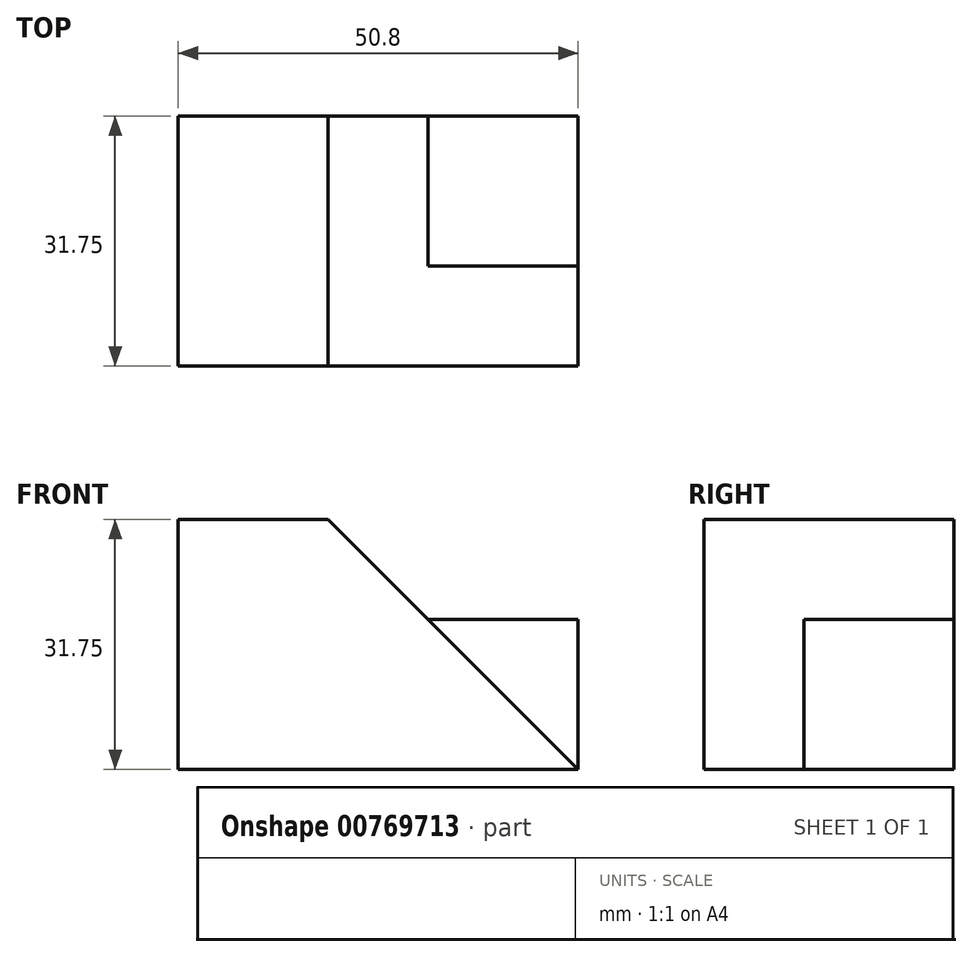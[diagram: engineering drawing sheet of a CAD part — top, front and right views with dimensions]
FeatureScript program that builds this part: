
annotation { "Feature Type Name" : "Feature", "Feature Type Description" : "" }
export const myFeature = defineFeature(function(context is Context, id is Id, definition is map)
    precondition{}
    {
        {
            var Q0;
            Q0=qCreatedBy(makeId("Front.planeOp"),FACE);
            var sketch = newSketch(context, id + "F0", { "sketchPlane" : qUnion([Q0])});
            skLineSegment(sketch, "E0", {"start": v(0, 0) * mm, "end": v(50.8, 0) * mm});
            skLineSegment(sketch, "E1", {"start": v(0, 0) * mm, "end": v(0, 31.75) * mm});
            skLineSegment(sketch, "E2", {"start": v(0, 31.75) * mm, "end": v(19.05, 31.75) * mm});
            skLineSegment(sketch, "E3", {"start": v(19.05, 31.75) * mm, "end": v(50.8, 0) * mm});
            skLineSegment(sketch, "E4", {"start": v(50.8, 0) * mm, "end": v(50.8, 19.05) * mm});
            skLineSegment(sketch, "E5", {"start": v(50.8, 19.05) * mm, "end": v(31.75, 19.05) * mm});
            skSolve(sketch);
        }
        {
            var Q0;
            {var subQ3=sQuery(id+"F0.wireOp",EDGE,"E0");Q0=makeQuery(id+"F0.imprint","IMPRINT",FACE,{"disambiguationData":[TD([[makeQuery(id+"F0.imprint","IMPRINT",EDGE,{"derivedFrom":subQ3}),1.0]])]});}
            extrude(context, id + "F1", {"entities" : qUnion([Q0]), "depth" : -31.75 * mm, "offsetDistance" : 25.4 * mm});
        }
        {
            var Q0;
            {var subQ0=sQuery(id+"F0.wireOp",EDGE,"E4");Q0=makeQuery(id+"F0.imprint","IMPRINT",FACE,{"disambiguationData":[TD([[makeQuery(id+"F0.imprint","IMPRINT",EDGE,{"derivedFrom":subQ0}),1.0]])]});}
            extrude(context, id + "F2", {"entities" : qUnion([Q0]), "operationType" : NewBodyOperationType.ADD, "depth" : -31.75 * mm, "offsetDistance" : 25.4 * mm});
        }
        {
            var Q0;
            {var subQ0=sQuery(id+"F0.wireOp",EDGE,"E4");Q0=makeQuery(id+"F0.imprint","IMPRINT",FACE,{"disambiguationData":[TD([[makeQuery(id+"F0.imprint","IMPRINT",EDGE,{"derivedFrom":subQ0}),1.0]])]});}
            extrude(context, id + "F3", {"entities" : qUnion([Q0]), "operationType" : NewBodyOperationType.REMOVE, "oppositeDirection" : true, "depth" : 12.7 * mm, "offsetDistance" : 25.4 * mm});
        }
    });
